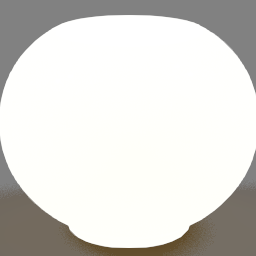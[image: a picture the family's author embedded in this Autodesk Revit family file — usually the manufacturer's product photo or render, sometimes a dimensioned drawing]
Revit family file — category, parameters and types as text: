
# Revit family: 3-5053-xx-xx Axiom Wall Sconce
name_source: partatom
category: Luminarias
units: mm (PartAtom-declared; Revit-internal decimal feet)

## family parameters
Anfitrión = Muro
Compartido = No
Corte con vacíos al cargar = No
Cota de conector redondo = Diámetro de uso
Número OmniClass = 23.80.70.00
Origen de luz = Sí
Punto de cálculo de habitación = No
Siempre vertical = Sí
Tipo de pieza = Normal
Título OmniClass = Lighting

## types (2) — shared parameters
Archivo de red fotométrica = 3-5053-40 Axiom 4LT.ies
Cambio de temperatura de color de luz atenuada = <Ninguno>
Comentarios de vataje = 1 x 12.0 W at 120 V
Diffuser = Ice Acrylic
Fabricante = Oxygen Lighting and Fans
Filtro de color = 16777215
Lámpara = LED Array
Modelo = 3-5053-xx / Axiom Wall Sconce
References = Ref. 3 = 120 V / Ref. 37 = 277 V
URL = www.oxygenlighting.com
Voltage = 120 V
Voltage Input = 120 V or 277 V - 50/60 Hz
Ángulo de inclinación = 90.00°
zero-valued in all types: Elevación por defecto

## per-type parameters (varying)
| type | Metal Finish 1 |
| 3-5053-15 / Black - ice acrylic | 15 - Black |
| 3-5053-40 / Aged Brass - Ice Acrylic | 40 - Aged Brass |

## geometry (parser evidence)
native form markers: Sweep x4
no freeform markers — native parametric forms only
